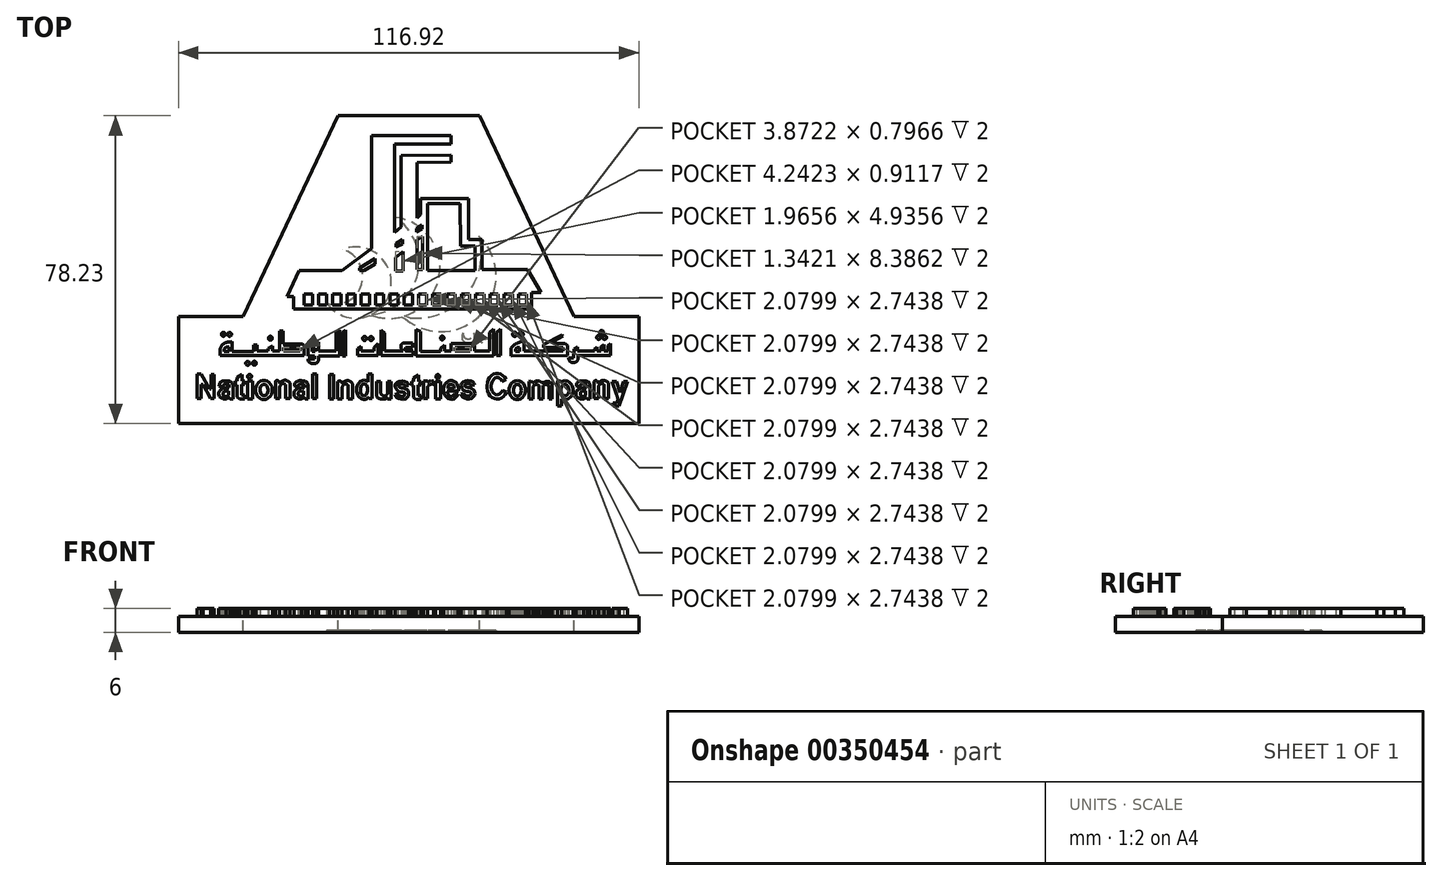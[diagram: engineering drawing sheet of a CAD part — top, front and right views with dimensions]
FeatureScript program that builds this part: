
annotation { "Feature Type Name" : "Feature", "Feature Type Description" : "" }
export const myFeature = defineFeature(function(context is Context, id is Id, definition is map)
    precondition{}
    {
        {
            var Q0;
            Q0=qCreatedBy(makeId("Top.planeOp"),FACE);
            var sketch = newSketch(context, id + "F0", { "sketchPlane" : qUnion([Q0])});
            skCircle(sketch, "E0", {"center": v(48.24, -1.08) * mm, "radius": 0.5 * mm});
            skLineSegment(sketch, "E1", {"start": v(48.24, -1.08) * mm, "end": v(49, 0.22) * mm, "construction": true});
            skLineSegment(sketch, "E2", {"start": v(49, 0.22) * mm, "end": v(49.74, -1.08) * mm, "construction": true});
            skLineSegment(sketch, "E3", {"start": v(49.74, -1.08) * mm, "end": v(48.24, -1.08) * mm, "construction": true});
            skCircle(sketch, "E4", {"center": v(49, 0.22) * mm, "radius": 0.5 * mm});
            skCircle(sketch, "E5", {"center": v(49.74, -1.08) * mm, "radius": 0.5 * mm});
            skLineSegment(sketch, "E6", {"start": v(51.29, -2.6) * mm, "end": v(51.29, -5.68) * mm});
            skLineSegment(sketch, "E7", {"start": v(51.29, -5.68) * mm, "end": v(43.03, -5.68) * mm});
            skLineSegment(sketch, "E8", {"start": v(43.03, -5.68) * mm, "end": v(43.03, -6.28) * mm});
            skArc(sketch, "E9", {"start": v(40.6, -6.28) * mm, "mid": v(41.82, -7.5) * mm, "end": v(43.03, -6.28) * mm});
            skLineSegment(sketch, "E10", {"start": v(51.29, -2.6) * mm, "end": v(50.58, -3.14) * mm});
            skLineSegment(sketch, "E11", {"start": v(50.58, -3.14) * mm, "end": v(50.58, -4.57) * mm});
            skLineSegment(sketch, "E12", {"start": v(50.58, -4.57) * mm, "end": v(49.56, -4.57) * mm});
            skLineSegment(sketch, "E13", {"start": v(49.56, -4.57) * mm, "end": v(49.56, -2.85) * mm});
            skLineSegment(sketch, "E14", {"start": v(49.56, -2.85) * mm, "end": v(48.86, -3.4) * mm});
            skLineSegment(sketch, "E15", {"start": v(48.86, -3.4) * mm, "end": v(48.86, -4.57) * mm});
            skLineSegment(sketch, "E16", {"start": v(48.86, -4.57) * mm, "end": v(47.84, -4.57) * mm});
            skLineSegment(sketch, "E17", {"start": v(47.84, -4.57) * mm, "end": v(47.84, -3.53) * mm});
            skLineSegment(sketch, "E18", {"start": v(47.84, -3.53) * mm, "end": v(47.13, -4.08) * mm});
            skLineSegment(sketch, "E19", {"start": v(47.13, -4.08) * mm, "end": v(47.13, -4.57) * mm});
            skLineSegment(sketch, "E20", {"start": v(47.13, -4.57) * mm, "end": v(43.03, -4.57) * mm});
            skLineSegment(sketch, "E21", {"start": v(43.03, -4.57) * mm, "end": v(42.85, -4.57) * mm});
            skLineSegment(sketch, "E22", {"start": v(42.85, -4.57) * mm, "end": v(42.85, -3.53) * mm});
            skLineSegment(sketch, "E23", {"start": v(42.85, -3.53) * mm, "end": v(41.96, -3.97) * mm});
            skLineSegment(sketch, "E24", {"start": v(41.96, -3.97) * mm, "end": v(41.91, -6.28) * mm});
            skLineSegment(sketch, "E25", {"start": v(41.91, -6.28) * mm, "end": v(40.6, -6.28) * mm});
            skLineSegment(sketch, "E26", {"start": v(47.13, -4.57) * mm, "end": v(47.84, -4.57) * mm, "construction": true});
            skLineSegment(sketch, "E27", {"start": v(48.86, -4.57) * mm, "end": v(49.56, -4.57) * mm, "construction": true});
            skLineSegment(sketch, "E28", {"start": v(50.58, -4.57) * mm, "end": v(51.29, -4.57) * mm, "construction": true});
            skLineSegment(sketch, "E29", {"start": v(39.17, -0.76) * mm, "end": v(36.88, -2.01) * mm});
            skLineSegment(sketch, "E30", {"start": v(36.88, -2.01) * mm, "end": v(36.88, -2.66) * mm});
            skLineSegment(sketch, "E31", {"start": v(36.88, -2.66) * mm, "end": v(39.68, -2.66) * mm});
            skLineSegment(sketch, "E32", {"start": v(39.68, -2.66) * mm, "end": v(40.3, -3.18) * mm});
            skLineSegment(sketch, "E33", {"start": v(40.3, -3.18) * mm, "end": v(40.3, -5.7) * mm});
            skLineSegment(sketch, "E34", {"start": v(40.3, -5.7) * mm, "end": v(26.05, -5.82) * mm});
            skLineSegment(sketch, "E35", {"start": v(26.05, -5.82) * mm, "end": v(26.03, -3.72) * mm});
            skLineSegment(sketch, "E36", {"start": v(39.17, -0.76) * mm, "end": v(38.98, -0.41) * mm});
            skLineSegment(sketch, "E37", {"start": v(38.98, -0.41) * mm, "end": v(34.18, -2.85) * mm});
            skLineSegment(sketch, "E38", {"start": v(34.18, -2.85) * mm, "end": v(34.18, -3.65) * mm});
            skLineSegment(sketch, "E39", {"start": v(34.18, -3.65) * mm, "end": v(39.17, -3.65) * mm});
            skLineSegment(sketch, "E40", {"start": v(39.17, -3.65) * mm, "end": v(39.17, -4.5) * mm});
            skLineSegment(sketch, "E41", {"start": v(39.17, -4.5) * mm, "end": v(29.33, -4.5) * mm});
            skLineSegment(sketch, "E42", {"start": v(29.33, -4.5) * mm, "end": v(29.33, -2.06) * mm});
            skCircle(sketch, "E43", {"center": v(28.57, -0.28) * mm, "radius": 0.55 * mm});
            skCircle(sketch, "E44", {"center": v(26.92, -0.3) * mm, "radius": 0.55 * mm});
            skFitSpline(sketch, "E45", {"points": [v(26.03, -3.72) * mm, v(26.74, -2.98) * mm, v(27.83, -2.4) * mm, v(28.7, -2.13) * mm, v(29.33, -2.06) * mm], "startDerivative": vector(2.44, 2.98) * mm, "endDerivative": vector(2.97, 0.2) * mm});
            skLineSegment(sketch, "E46", {"start": v(23.3, 1.06) * mm, "end": v(22.3, 0.2) * mm});
            skLineSegment(sketch, "E47", {"start": v(22.3, 0.2) * mm, "end": v(22.3, -5.68) * mm});
            skLineSegment(sketch, "E48", {"start": v(22.3, -5.68) * mm, "end": v(23.3, -5.68) * mm});
            skLineSegment(sketch, "E49", {"start": v(23.3, -5.68) * mm, "end": v(23.3, 1.06) * mm});
            skLineSegment(sketch, "E50", {"start": v(21.48, 1.06) * mm, "end": v(20.48, 0.2) * mm});
            skLineSegment(sketch, "E51", {"start": v(20.48, 0.2) * mm, "end": v(20.48, -4.58) * mm});
            skLineSegment(sketch, "E52", {"start": v(20.48, -4.58) * mm, "end": v(16.7, -4.58) * mm});
            skLineSegment(sketch, "E53", {"start": v(16.7, -4.58) * mm, "end": v(16.7, -2.63) * mm});
            skLineSegment(sketch, "E54", {"start": v(16.7, -2.63) * mm, "end": v(10.79, -2.63) * mm});
            skLineSegment(sketch, "E55", {"start": v(10.79, -2.63) * mm, "end": v(10.79, -4.58) * mm});
            skLineSegment(sketch, "E56", {"start": v(10.79, -4.58) * mm, "end": v(9.15, -4.58) * mm});
            skLineSegment(sketch, "E57", {"start": v(9.15, -4.58) * mm, "end": v(9.15, -3.05) * mm});
            skLineSegment(sketch, "E58", {"start": v(9.15, -3.05) * mm, "end": v(8.13, -3.92) * mm});
            skLineSegment(sketch, "E59", {"start": v(8.13, -3.92) * mm, "end": v(8.13, -4.62) * mm});
            skLineSegment(sketch, "E60", {"start": v(8.13, -4.62) * mm, "end": v(2.96, -4.62) * mm});
            skLineSegment(sketch, "E61", {"start": v(2.96, -4.62) * mm, "end": v(2.96, 0.45) * mm});
            skLineSegment(sketch, "E62", {"start": v(2.96, 0.45) * mm, "end": v(1.87, 0.89) * mm});
            skLineSegment(sketch, "E63", {"start": v(1.87, 0.89) * mm, "end": v(1.87, -5.75) * mm});
            skLineSegment(sketch, "E64", {"start": v(1.87, -5.75) * mm, "end": v(21.48, -5.75) * mm});
            skLineSegment(sketch, "E65", {"start": v(21.48, -5.75) * mm, "end": v(21.48, 1.06) * mm});
            skCircle(sketch, "E66", {"center": v(8.49, -1.21) * mm, "radius": 0.47 * mm});
            skLineSegment(sketch, "E67", {"start": v(11.74, -4.47) * mm, "end": v(11.74, -3.67) * mm});
            skLineSegment(sketch, "E68", {"start": v(11.74, -3.67) * mm, "end": v(15.61, -3.67) * mm});
            skLineSegment(sketch, "E69", {"start": v(15.61, -3.67) * mm, "end": v(15.61, -4.47) * mm});
            skLineSegment(sketch, "E70", {"start": v(15.61, -4.47) * mm, "end": v(11.74, -4.47) * mm});
            skLineSegment(sketch, "E71", {"start": v(0.99, -2.48) * mm, "end": v(-1.42, -2.48) * mm});
            skLineSegment(sketch, "E72", {"start": v(0.99, -2.48) * mm, "end": v(0.99, -3.64) * mm});
            skLineSegment(sketch, "E73", {"start": v(0.99, -3.64) * mm, "end": v(-0.78, -3.64) * mm});
            skFitSpline(sketch, "E74", {"points": [v(-1.42, -2.48) * mm, v(-1.9, -2.92) * mm, v(-1.95, -3.8) * mm, v(-1.42, -4.55) * mm], "startDerivative": vector(-1.87, -1.2) * mm, "endDerivative": vector(1.85, -1.92) * mm});
            skFitSpline(sketch, "E75", {"points": [v(-0.78, -3.64) * mm, v(-0.95, -4.14) * mm, v(-0.78, -4.58) * mm], "startDerivative": vector(-0.53, -0.99) * mm, "endDerivative": vector(0.54, -0.9) * mm});
            skLineSegment(sketch, "E76", {"start": v(-0.78, -4.58) * mm, "end": v(1.11, -4.58) * mm});
            skLineSegment(sketch, "E77", {"start": v(1.11, -4.58) * mm, "end": v(1.11, -5.7) * mm});
            skLineSegment(sketch, "E78", {"start": v(1.11, -5.7) * mm, "end": v(-7.1, -5.7) * mm});
            skLineSegment(sketch, "E79", {"start": v(-7.1, -5.7) * mm, "end": v(-7.1, 0.87) * mm});
            skLineSegment(sketch, "E80", {"start": v(-7.1, 0.87) * mm, "end": v(-6.1, 0.09) * mm});
            skLineSegment(sketch, "E81", {"start": v(-6.1, 0.09) * mm, "end": v(-6.1, -4.58) * mm});
            skLineSegment(sketch, "E82", {"start": v(-6.1, -4.58) * mm, "end": v(-1.42, -4.55) * mm});
            skLineSegment(sketch, "E83", {"start": v(-7.78, -2.61) * mm, "end": v(-8.87, -3.6) * mm});
            skLineSegment(sketch, "E84", {"start": v(-8.87, -3.6) * mm, "end": v(-8.87, -4.55) * mm});
            skLineSegment(sketch, "E85", {"start": v(-8.87, -4.55) * mm, "end": v(-12.15, -4.55) * mm});
            skLineSegment(sketch, "E86", {"start": v(-12.15, -4.55) * mm, "end": v(-12.15, -3.32) * mm});
            skLineSegment(sketch, "E87", {"start": v(-12.15, -3.32) * mm, "end": v(-13.02, -3.88) * mm});
            skLineSegment(sketch, "E88", {"start": v(-13.02, -3.88) * mm, "end": v(-13.02, -5.71) * mm});
            skLineSegment(sketch, "E89", {"start": v(-13.02, -5.71) * mm, "end": v(-7.78, -5.71) * mm});
            skLineSegment(sketch, "E90", {"start": v(-7.78, -5.71) * mm, "end": v(-7.78, -2.61) * mm});
            skCircle(sketch, "E91", {"center": v(-9.58, -1.38) * mm, "radius": 0.5 * mm});
            skCircle(sketch, "E92", {"center": v(-11.22, -1.35) * mm, "radius": 0.5 * mm});
            skLineSegment(sketch, "E93", {"start": v(-16, 0.78) * mm, "end": v(-16, -5.74) * mm});
            skLineSegment(sketch, "E94", {"start": v(-16, -5.74) * mm, "end": v(-16.83, -5.74) * mm});
            skLineSegment(sketch, "E95", {"start": v(-16.83, -5.74) * mm, "end": v(-16.83, 0.25) * mm});
            skLineSegment(sketch, "E96", {"start": v(-16.83, 0.25) * mm, "end": v(-16, 0.78) * mm});
            skLineSegment(sketch, "E97", {"start": v(-17.63, 0.78) * mm, "end": v(-17.63, -5.74) * mm});
            skLineSegment(sketch, "E98", {"start": v(-17.63, -5.74) * mm, "end": v(-22.85, -5.74) * mm});
            skLineSegment(sketch, "E99", {"start": v(-22.85, -5.74) * mm, "end": v(-22.85, -6.67) * mm});
            skLineSegment(sketch, "E100", {"start": v(-17.63, 0.78) * mm, "end": v(-18.48, 0.25) * mm});
            skLineSegment(sketch, "E101", {"start": v(-18.48, 0.25) * mm, "end": v(-18.48, -4.5) * mm});
            skLineSegment(sketch, "E102", {"start": v(-18.48, -4.5) * mm, "end": v(-22.88, -4.5) * mm});
            skLineSegment(sketch, "E103", {"start": v(-22.88, -4.5) * mm, "end": v(-22.88, -2.25) * mm});
            skFitSpline(sketch, "E104", {"points": [v(-22.88, -2.25) * mm, v(-24.47, -2.52) * mm, v(-25.6, -3.51) * mm], "startDerivative": vector(-3.34, -0.16) * mm, "endDerivative": vector(-2.1, -2.38) * mm});
            skLineSegment(sketch, "E105", {"start": v(-25.6, -3.51) * mm, "end": v(-25.6, -5.85) * mm});
            skLineSegment(sketch, "E106", {"start": v(-25.6, -5.85) * mm, "end": v(-23.95, -5.85) * mm});
            skLineSegment(sketch, "E107", {"start": v(-23.95, -5.85) * mm, "end": v(-23.95, -6.54) * mm});
            skLineSegment(sketch, "E108", {"start": v(-23.95, -6.54) * mm, "end": v(-25.6, -6.54) * mm});
            skFitSpline(sketch, "E109", {"points": [v(-25.6, -6.54) * mm, v(-25.35, -7.3) * mm, v(-24.14, -7.74) * mm, v(-23.17, -7.4) * mm, v(-22.85, -6.67) * mm], "startDerivative": vector(0.39, -3.57) * mm, "endDerivative": vector(0.93, 3.52) * mm});
            skLineSegment(sketch, "E110", {"start": v(-23.83, -3.75) * mm, "end": v(-23.83, -4.67) * mm});
            skLineSegment(sketch, "E111", {"start": v(-23.83, -4.67) * mm, "end": v(-24.61, -4.67) * mm});
            skLineSegment(sketch, "E112", {"start": v(-24.61, -4.67) * mm, "end": v(-24.61, -3.75) * mm});
            skLineSegment(sketch, "E113", {"start": v(-24.61, -3.75) * mm, "end": v(-23.83, -3.75) * mm});
            skLineSegment(sketch, "E114", {"start": v(-31.85, -3.65) * mm, "end": v(-27.6, -3.65) * mm});
            skLineSegment(sketch, "E115", {"start": v(-27.6, -3.65) * mm, "end": v(-27.6, -4.56) * mm});
            skLineSegment(sketch, "E116", {"start": v(-27.6, -4.56) * mm, "end": v(-31.85, -4.56) * mm});
            skLineSegment(sketch, "E117", {"start": v(-31.85, -4.56) * mm, "end": v(-31.85, -3.65) * mm});
            skCircle(sketch, "E118", {"center": v(-39.24, -7.62) * mm, "radius": 0.5 * mm});
            skCircle(sketch, "E119", {"center": v(-40.93, -7.65) * mm, "radius": 0.5 * mm});
            skCircle(sketch, "E120", {"center": v(-35.16, -1.27) * mm, "radius": 0.5 * mm});
            skCircle(sketch, "E121", {"center": v(-45.52, -0.3) * mm, "radius": 0.5 * mm});
            skCircle(sketch, "E122", {"center": v(-47.11, -0.3) * mm, "radius": 0.5 * mm});
            skLineSegment(sketch, "E123", {"start": v(28.2, -3.6) * mm, "end": v(28.2, -4.62) * mm});
            skLineSegment(sketch, "E124", {"start": v(28.2, -4.62) * mm, "end": v(27.09, -4.62) * mm});
            skLineSegment(sketch, "E125", {"start": v(27.09, -4.62) * mm, "end": v(27.09, -3.97) * mm});
            skLineSegment(sketch, "E126", {"start": v(27.09, -3.97) * mm, "end": v(27.54, -3.6) * mm});
            skLineSegment(sketch, "E127", {"start": v(27.54, -3.6) * mm, "end": v(28.2, -3.6) * mm});
            skLineSegment(sketch, "E128", {"start": v(-31.92, 0.6) * mm, "end": v(-31.92, -2.78) * mm});
            skLineSegment(sketch, "E129", {"start": v(-31.92, -2.78) * mm, "end": v(-27.02, -2.78) * mm});
            skLineSegment(sketch, "E130", {"start": v(-27.02, -2.78) * mm, "end": v(-26.56, -3.22) * mm});
            skLineSegment(sketch, "E131", {"start": v(-26.56, -3.22) * mm, "end": v(-26.56, -5.66) * mm});
            skLineSegment(sketch, "E132", {"start": v(-26.56, -5.66) * mm, "end": v(-47.89, -5.66) * mm});
            skLineSegment(sketch, "E133", {"start": v(-47.89, -5.66) * mm, "end": v(-47.89, -3.85) * mm});
            skFitSpline(sketch, "E134", {"points": [v(-47.89, -3.85) * mm, v(-47.42, -3.03) * mm, v(-46.55, -2.42) * mm, v(-44.91, -2.17) * mm], "startDerivative": vector(1.34, 2.92) * mm, "endDerivative": vector(4.5, 0.32) * mm});
            skLineSegment(sketch, "E135", {"start": v(-44.91, -2.17) * mm, "end": v(-44.91, -4.6) * mm});
            skLineSegment(sketch, "E136", {"start": v(-44.91, -4.6) * mm, "end": v(-39.44, -4.6) * mm});
            skLineSegment(sketch, "E137", {"start": v(-39.44, -4.6) * mm, "end": v(-39.44, -3) * mm});
            skLineSegment(sketch, "E138", {"start": v(-39.44, -3) * mm, "end": v(-38.57, -3) * mm});
            skLineSegment(sketch, "E139", {"start": v(-38.57, -3) * mm, "end": v(-38.57, -4.52) * mm});
            skLineSegment(sketch, "E140", {"start": v(-38.57, -4.52) * mm, "end": v(-35.7, -4.52) * mm});
            skLineSegment(sketch, "E141", {"start": v(-35.7, -4.52) * mm, "end": v(-35.7, -3.94) * mm});
            skLineSegment(sketch, "E142", {"start": v(-35.7, -3.94) * mm, "end": v(-34.6, -3.2) * mm});
            skLineSegment(sketch, "E143", {"start": v(-34.6, -3.2) * mm, "end": v(-34.6, -4.52) * mm});
            skLineSegment(sketch, "E144", {"start": v(-34.6, -4.52) * mm, "end": v(-32.85, -4.52) * mm});
            skLineSegment(sketch, "E145", {"start": v(-32.85, -4.52) * mm, "end": v(-32.85, 0.6) * mm});
            skLineSegment(sketch, "E146", {"start": v(-32.85, 0.6) * mm, "end": v(-31.92, 0.6) * mm});
            skLineSegment(sketch, "E147", {"start": v(-45.68, -3.54) * mm, "end": v(-45.68, -4.68) * mm});
            skLineSegment(sketch, "E148", {"start": v(-45.68, -4.68) * mm, "end": v(-46.94, -4.68) * mm});
            skLineSegment(sketch, "E149", {"start": v(-46.94, -4.68) * mm, "end": v(-46.94, -3.97) * mm});
            skLineSegment(sketch, "E150", {"start": v(-46.94, -3.97) * mm, "end": v(-46.4, -3.54) * mm});
            skLineSegment(sketch, "E151", {"start": v(-46.4, -3.54) * mm, "end": v(-45.68, -3.54) * mm});
            skLineSegment(sketch, "E152", {"start": v(-53.75, -16.57) * mm, "end": v(-53.75, -10.42) * mm});
            skLineSegment(sketch, "E153", {"start": v(-53.75, -10.42) * mm, "end": v(-52.77, -10.42) * mm});
            skLineSegment(sketch, "E154", {"start": v(-52.77, -10.42) * mm, "end": v(-50.6, -14.14) * mm});
            skLineSegment(sketch, "E155", {"start": v(-50.6, -14.14) * mm, "end": v(-50.16, -14.14) * mm});
            skLineSegment(sketch, "E156", {"start": v(-50.16, -14.14) * mm, "end": v(-50.16, -10.46) * mm});
            skLineSegment(sketch, "E157", {"start": v(-50.16, -10.46) * mm, "end": v(-49.4, -10.46) * mm});
            skLineSegment(sketch, "E158", {"start": v(-49.4, -10.46) * mm, "end": v(-49.4, -16.57) * mm});
            skLineSegment(sketch, "E159", {"start": v(-49.4, -16.57) * mm, "end": v(-50.4, -16.57) * mm});
            skLineSegment(sketch, "E160", {"start": v(-50.4, -16.57) * mm, "end": v(-52.24, -12.99) * mm});
            skLineSegment(sketch, "E161", {"start": v(-52.24, -12.99) * mm, "end": v(-52.71, -12.99) * mm});
            skLineSegment(sketch, "E162", {"start": v(-52.71, -12.99) * mm, "end": v(-52.71, -16.57) * mm});
            skLineSegment(sketch, "E163", {"start": v(-52.71, -16.57) * mm, "end": v(-53.75, -16.57) * mm});
            skLineSegment(sketch, "E164", {"start": v(-45.82, -14.69) * mm, "end": v(-45.82, -15.71) * mm});
            skFitSpline(sketch, "E165", {"points": [v(-45.82, -15.71) * mm, v(-46.28, -16.01) * mm, v(-47.04, -15.86) * mm, v(-47.16, -15.4) * mm, v(-47.11, -15.03) * mm, v(-46.68, -14.73) * mm, v(-46.18, -14.62) * mm], "startDerivative": vector(-2.15, -2.28) * mm, "endDerivative": vector(2.93, 1.5) * mm});
            skFitSpline(sketch, "E166", {"points": [v(-46.18, -14.62) * mm, v(-45.82, -14.69) * mm], "startDerivative": vector(0.32, -0.12) * mm, "endDerivative": vector(0.32, -0.12) * mm});
            skLineSegment(sketch, "E167", {"start": v(-44.69, -13.02) * mm, "end": v(-44.69, -16.74) * mm});
            skLineSegment(sketch, "E168", {"start": v(-44.69, -16.74) * mm, "end": v(-45.34, -16.74) * mm});
            skFitSpline(sketch, "E169", {"points": [v(-45.34, -16.74) * mm, v(-45.71, -16.4) * mm, v(-46.37, -16.74) * mm], "startDerivative": vector(-0.73, 1.05) * mm, "endDerivative": vector(-1.3, -0.98) * mm});
            skFitSpline(sketch, "E170", {"points": [v(-46.37, -16.74) * mm, v(-47.07, -16.74) * mm, v(-47.72, -16.42) * mm, v(-48.19, -15.96) * mm, v(-48.23, -15.03) * mm, v(-47.93, -14.5) * mm, v(-47.53, -14.19) * mm, v(-47.32, -14.1) * mm, v(-47.04, -13.97) * mm, v(-46.24, -13.85) * mm], "startDerivative": vector(-5.8, -0.65) * mm, "endDerivative": vector(6.93, 0.53) * mm});
            skLineSegment(sketch, "E171", {"start": v(-46.24, -13.85) * mm, "end": v(-45.6, -13.85) * mm});
            skLineSegment(sketch, "E172", {"start": v(-45.6, -13.85) * mm, "end": v(-45.6, -13.13) * mm});
            skFitSpline(sketch, "E173", {"points": [v(-44.69, -13.02) * mm, v(-44.95, -12.55) * mm, v(-45.52, -12.2) * mm, v(-46.4, -12.09) * mm, v(-47.26, -12.16) * mm, v(-47.99, -12.65) * mm, v(-48.13, -13.13) * mm, v(-48.14, -13.47) * mm], "startDerivative": vector(-1.65, 3.82) * mm, "endDerivative": vector(-0.04, -3.2) * mm});
            skFitSpline(sketch, "E174", {"points": [v(-48.14, -13.47) * mm, v(-47.32, -13.47) * mm, v(-47.17, -13.26) * mm, v(-46.9, -13.02) * mm, v(-46.4, -12.9) * mm, v(-45.9, -12.96) * mm, v(-45.6, -13.13) * mm], "startDerivative": vector(4.5, -0.54) * mm, "endDerivative": vector(1.87, -1.28) * mm});
            skLineSegment(sketch, "E175", {"start": v(-40.98, -12.19) * mm, "end": v(-40.98, -16.68) * mm});
            skLineSegment(sketch, "E176", {"start": v(-40.98, -16.68) * mm, "end": v(-39.74, -16.68) * mm});
            skLineSegment(sketch, "E177", {"start": v(-39.74, -16.68) * mm, "end": v(-39.74, -12.19) * mm});
            skLineSegment(sketch, "E178", {"start": v(-39.74, -12.19) * mm, "end": v(-40.98, -12.19) * mm});
            skCircle(sketch, "E179", {"center": v(-40.45, -10.98) * mm, "radius": 0.5 * mm});
            skEllipse(sketch, "E180", {"center": v(-36.8, -14.42) * mm, "majorRadius": 1.44 * mm, "minorRadius": 1.03 * mm, "majorAxis": v(0, -1)});
            skEllipse(sketch, "E181", {"center": v(-36.8, -14.42) * mm, "majorRadius": 2.46 * mm, "minorRadius": 2.13 * mm, "majorAxis": v(0, -1)});
            skLineSegment(sketch, "E182", {"start": v(-33.88, -12.24) * mm, "end": v(-33.88, -16.58) * mm});
            skLineSegment(sketch, "E183", {"start": v(-33.88, -16.58) * mm, "end": v(-32.78, -16.58) * mm});
            skLineSegment(sketch, "E184", {"start": v(-32.78, -16.58) * mm, "end": v(-32.78, -13.6) * mm});
            skFitSpline(sketch, "E185", {"points": [v(-32.78, -13.6) * mm, v(-32.45, -13.03) * mm, v(-31.9, -12.78) * mm, v(-31.27, -13.08) * mm], "startDerivative": vector(0.82, 1.83) * mm, "endDerivative": vector(1.83, -1.27) * mm});
            skLineSegment(sketch, "E186", {"start": v(-31.27, -13.08) * mm, "end": v(-31.27, -16.58) * mm});
            skLineSegment(sketch, "E187", {"start": v(-31.27, -16.58) * mm, "end": v(-30.12, -16.58) * mm});
            skLineSegment(sketch, "E188", {"start": v(-30.12, -16.58) * mm, "end": v(-30.12, -12.81) * mm});
            skFitSpline(sketch, "E189", {"points": [v(-33.88, -12.24) * mm, v(-33.45, -12) * mm, v(-32.9, -12.34) * mm, v(-32.8, -12.73) * mm], "startDerivative": vector(1.19, 1.08) * mm, "endDerivative": vector(0.02, -1.32) * mm});
            skFitSpline(sketch, "E190", {"points": [v(-30.12, -12.81) * mm, v(-30.6, -12.24) * mm, v(-31.34, -11.95) * mm, v(-31.81, -12) * mm, v(-32.3, -12.24) * mm, v(-32.8, -12.73) * mm], "startDerivative": vector(-1.86, 2.95) * mm, "endDerivative": vector(-2.36, -2.6) * mm});
            skLineSegment(sketch, "E191", {"start": v(-26.73, -14.67) * mm, "end": v(-26.73, -15.7) * mm});
            skFitSpline(sketch, "E192", {"points": [v(-26.73, -15.7) * mm, v(-27.2, -16) * mm, v(-27.96, -15.85) * mm, v(-28.07, -15.4) * mm, v(-28.03, -15.02) * mm, v(-27.6, -14.72) * mm, v(-27.1, -14.6) * mm], "startDerivative": vector(-2.15, -2.28) * mm, "endDerivative": vector(2.93, 1.5) * mm});
            skFitSpline(sketch, "E193", {"points": [v(-27.1, -14.6) * mm, v(-26.73, -14.67) * mm], "startDerivative": vector(0.32, -0.12) * mm, "endDerivative": vector(0.32, -0.12) * mm});
            skLineSegment(sketch, "E194", {"start": v(-25.6, -13.01) * mm, "end": v(-25.6, -16.73) * mm});
            skLineSegment(sketch, "E195", {"start": v(-25.6, -16.73) * mm, "end": v(-26.26, -16.73) * mm});
            skFitSpline(sketch, "E196", {"points": [v(-26.26, -16.73) * mm, v(-26.63, -16.4) * mm, v(-27.29, -16.73) * mm], "startDerivative": vector(-0.73, 1.05) * mm, "endDerivative": vector(-1.3, -0.98) * mm});
            skFitSpline(sketch, "E197", {"points": [v(-27.29, -16.73) * mm, v(-27.98, -16.73) * mm, v(-28.64, -16.4) * mm, v(-29.1, -15.95) * mm, v(-29.15, -15.02) * mm, v(-28.85, -14.49) * mm, v(-28.44, -14.18) * mm, v(-28.24, -14.1) * mm, v(-27.96, -13.96) * mm, v(-27.16, -13.84) * mm], "startDerivative": vector(-5.8, -0.65) * mm, "endDerivative": vector(6.93, 0.53) * mm});
            skLineSegment(sketch, "E198", {"start": v(-27.16, -13.84) * mm, "end": v(-26.51, -13.84) * mm});
            skLineSegment(sketch, "E199", {"start": v(-26.51, -13.84) * mm, "end": v(-26.51, -13.11) * mm});
            skFitSpline(sketch, "E200", {"points": [v(-25.6, -13.01) * mm, v(-25.87, -12.54) * mm, v(-26.43, -12.18) * mm, v(-27.31, -12.07) * mm, v(-28.18, -12.14) * mm, v(-28.9, -12.64) * mm, v(-29.04, -13.11) * mm, v(-29.06, -13.46) * mm], "startDerivative": vector(-1.65, 3.82) * mm, "endDerivative": vector(-0.04, -3.2) * mm});
            skFitSpline(sketch, "E201", {"points": [v(-29.06, -13.46) * mm, v(-28.24, -13.46) * mm, v(-28.09, -13.25) * mm, v(-27.82, -13.01) * mm, v(-27.31, -12.9) * mm, v(-26.81, -12.95) * mm, v(-26.51, -13.11) * mm], "startDerivative": vector(4.5, -0.54) * mm, "endDerivative": vector(1.87, -1.28) * mm});
            skLineSegment(sketch, "E202", {"start": v(-18.03, -12.33) * mm, "end": v(-18.03, -16.68) * mm});
            skLineSegment(sketch, "E203", {"start": v(-18.03, -16.68) * mm, "end": v(-16.94, -16.68) * mm});
            skLineSegment(sketch, "E204", {"start": v(-16.94, -16.68) * mm, "end": v(-16.94, -13.7) * mm});
            skFitSpline(sketch, "E205", {"points": [v(-16.94, -13.7) * mm, v(-16.6, -13.13) * mm, v(-16.06, -12.88) * mm, v(-15.42, -13.18) * mm], "startDerivative": vector(0.82, 1.83) * mm, "endDerivative": vector(1.83, -1.27) * mm});
            skLineSegment(sketch, "E206", {"start": v(-15.42, -13.18) * mm, "end": v(-15.42, -16.68) * mm});
            skLineSegment(sketch, "E207", {"start": v(-15.42, -16.68) * mm, "end": v(-14.28, -16.68) * mm});
            skLineSegment(sketch, "E208", {"start": v(-14.28, -16.68) * mm, "end": v(-14.28, -12.91) * mm});
            skFitSpline(sketch, "E209", {"points": [v(-18.03, -12.33) * mm, v(-17.6, -12.1) * mm, v(-17.05, -12.44) * mm, v(-16.96, -12.83) * mm], "startDerivative": vector(1.19, 1.08) * mm, "endDerivative": vector(0.02, -1.32) * mm});
            skFitSpline(sketch, "E210", {"points": [v(-14.28, -12.91) * mm, v(-14.75, -12.33) * mm, v(-15.5, -12.04) * mm, v(-15.97, -12.1) * mm, v(-16.45, -12.33) * mm, v(-16.96, -12.83) * mm], "startDerivative": vector(-1.86, 2.95) * mm, "endDerivative": vector(-2.36, -2.6) * mm});
            skLineSegment(sketch, "E211", {"start": v(-23.45, -10.43) * mm, "end": v(-23.45, -16.65) * mm});
            skLineSegment(sketch, "E212", {"start": v(-23.45, -16.65) * mm, "end": v(-24.5, -16.65) * mm});
            skLineSegment(sketch, "E213", {"start": v(-24.5, -16.65) * mm, "end": v(-24.5, -10.43) * mm});
            skLineSegment(sketch, "E214", {"start": v(-24.5, -10.43) * mm, "end": v(-23.45, -10.43) * mm});
            skLineSegment(sketch, "E215", {"start": v(-19.09, -10.51) * mm, "end": v(-19.09, -16.73) * mm});
            skLineSegment(sketch, "E216", {"start": v(-19.09, -16.73) * mm, "end": v(-20.14, -16.73) * mm});
            skLineSegment(sketch, "E217", {"start": v(-20.14, -16.73) * mm, "end": v(-20.14, -10.51) * mm});
            skLineSegment(sketch, "E218", {"start": v(-20.14, -10.51) * mm, "end": v(-19.09, -10.51) * mm});
            skLineSegment(sketch, "E219", {"start": v(-42.4, -10.53) * mm, "end": v(-43.58, -11.24) * mm});
            skLineSegment(sketch, "E220", {"start": v(-43.58, -11.24) * mm, "end": v(-43.58, -12.11) * mm});
            skLineSegment(sketch, "E221", {"start": v(-43.58, -12.11) * mm, "end": v(-44.07, -12.11) * mm});
            skLineSegment(sketch, "E222", {"start": v(-44.07, -12.11) * mm, "end": v(-44.07, -13.14) * mm});
            skLineSegment(sketch, "E223", {"start": v(-44.07, -13.14) * mm, "end": v(-43.61, -13.14) * mm});
            skLineSegment(sketch, "E224", {"start": v(-43.61, -13.14) * mm, "end": v(-43.61, -16.26) * mm});
            skLineSegment(sketch, "E225", {"start": v(-43.61, -16.26) * mm, "end": v(-42.98, -16.7) * mm});
            skLineSegment(sketch, "E226", {"start": v(-42.98, -16.7) * mm, "end": v(-41.67, -16.7) * mm});
            skLineSegment(sketch, "E227", {"start": v(-41.67, -16.7) * mm, "end": v(-41.67, -15.74) * mm});
            skLineSegment(sketch, "E228", {"start": v(-41.67, -15.74) * mm, "end": v(-42.42, -15.74) * mm});
            skLineSegment(sketch, "E229", {"start": v(-42.42, -15.74) * mm, "end": v(-42.42, -13.06) * mm});
            skLineSegment(sketch, "E230", {"start": v(-42.42, -13.06) * mm, "end": v(-41.66, -13.06) * mm});
            skLineSegment(sketch, "E231", {"start": v(-41.66, -13.06) * mm, "end": v(-41.66, -12.11) * mm});
            skLineSegment(sketch, "E232", {"start": v(-41.66, -12.11) * mm, "end": v(-42.4, -12.11) * mm});
            skLineSegment(sketch, "E233", {"start": v(-42.4, -12.11) * mm, "end": v(-42.4, -10.53) * mm});
            skLineSegment(sketch, "E234", {"start": v(2.43, -10.67) * mm, "end": v(1.25, -11.37) * mm});
            skLineSegment(sketch, "E235", {"start": v(1.25, -11.37) * mm, "end": v(1.25, -12.25) * mm});
            skLineSegment(sketch, "E236", {"start": v(1.25, -12.25) * mm, "end": v(0.77, -12.25) * mm});
            skLineSegment(sketch, "E237", {"start": v(0.77, -12.25) * mm, "end": v(0.77, -13.28) * mm});
            skLineSegment(sketch, "E238", {"start": v(0.77, -13.28) * mm, "end": v(1.22, -13.28) * mm});
            skLineSegment(sketch, "E239", {"start": v(1.22, -13.28) * mm, "end": v(1.22, -16.4) * mm});
            skLineSegment(sketch, "E240", {"start": v(1.22, -16.4) * mm, "end": v(1.86, -16.84) * mm});
            skLineSegment(sketch, "E241", {"start": v(1.86, -16.84) * mm, "end": v(3.16, -16.84) * mm});
            skLineSegment(sketch, "E242", {"start": v(3.16, -16.84) * mm, "end": v(3.16, -15.88) * mm});
            skLineSegment(sketch, "E243", {"start": v(3.16, -15.88) * mm, "end": v(2.42, -15.88) * mm});
            skLineSegment(sketch, "E244", {"start": v(2.42, -15.88) * mm, "end": v(2.42, -13.2) * mm});
            skLineSegment(sketch, "E245", {"start": v(2.42, -13.2) * mm, "end": v(3.18, -13.2) * mm});
            skLineSegment(sketch, "E246", {"start": v(3.18, -13.2) * mm, "end": v(3.18, -12.25) * mm});
            skLineSegment(sketch, "E247", {"start": v(3.18, -12.25) * mm, "end": v(2.43, -12.25) * mm});
            skLineSegment(sketch, "E248", {"start": v(2.43, -12.25) * mm, "end": v(2.43, -10.67) * mm});
            skLineSegment(sketch, "E249", {"start": v(44.92, -14.69) * mm, "end": v(44.92, -15.71) * mm});
            skFitSpline(sketch, "E250", {"points": [v(44.92, -15.71) * mm, v(44.46, -16.01) * mm, v(43.7, -15.86) * mm, v(43.58, -15.4) * mm, v(43.63, -15.03) * mm, v(44.06, -14.73) * mm, v(44.56, -14.62) * mm], "startDerivative": vector(-2.15, -2.28) * mm, "endDerivative": vector(2.93, 1.5) * mm});
            skFitSpline(sketch, "E251", {"points": [v(44.56, -14.62) * mm, v(44.92, -14.69) * mm], "startDerivative": vector(0.32, -0.12) * mm, "endDerivative": vector(0.32, -0.12) * mm});
            skLineSegment(sketch, "E252", {"start": v(46.05, -13.02) * mm, "end": v(46.05, -16.74) * mm});
            skLineSegment(sketch, "E253", {"start": v(46.05, -16.74) * mm, "end": v(45.4, -16.74) * mm});
            skFitSpline(sketch, "E254", {"points": [v(45.4, -16.74) * mm, v(45.03, -16.4) * mm, v(44.37, -16.74) * mm], "startDerivative": vector(-0.73, 1.05) * mm, "endDerivative": vector(-1.3, -0.98) * mm});
            skFitSpline(sketch, "E255", {"points": [v(44.37, -16.74) * mm, v(43.67, -16.74) * mm, v(43.02, -16.42) * mm, v(42.55, -15.96) * mm, v(42.5, -15.03) * mm, v(42.8, -14.5) * mm, v(43.21, -14.19) * mm, v(43.42, -14.1) * mm, v(43.7, -13.97) * mm, v(44.5, -13.85) * mm], "startDerivative": vector(-5.8, -0.65) * mm, "endDerivative": vector(6.93, 0.53) * mm});
            skLineSegment(sketch, "E256", {"start": v(44.5, -13.85) * mm, "end": v(45.14, -13.85) * mm});
            skLineSegment(sketch, "E257", {"start": v(45.14, -13.85) * mm, "end": v(45.14, -13.13) * mm});
            skFitSpline(sketch, "E258", {"points": [v(46.05, -13.02) * mm, v(45.79, -12.55) * mm, v(45.22, -12.2) * mm, v(44.34, -12.09) * mm, v(43.48, -12.16) * mm, v(42.75, -12.65) * mm, v(42.61, -13.13) * mm, v(42.6, -13.47) * mm], "startDerivative": vector(-1.65, 3.82) * mm, "endDerivative": vector(-0.04, -3.2) * mm});
            skFitSpline(sketch, "E259", {"points": [v(42.6, -13.47) * mm, v(43.42, -13.47) * mm, v(43.57, -13.26) * mm, v(43.84, -13.02) * mm, v(44.34, -12.9) * mm, v(44.85, -12.96) * mm, v(45.14, -13.13) * mm], "startDerivative": vector(4.5, -0.54) * mm, "endDerivative": vector(1.87, -1.28) * mm});
            skLineSegment(sketch, "E260", {"start": v(47.05, -12.25) * mm, "end": v(47.05, -16.6) * mm});
            skLineSegment(sketch, "E261", {"start": v(47.05, -16.6) * mm, "end": v(48.15, -16.6) * mm});
            skLineSegment(sketch, "E262", {"start": v(48.15, -16.6) * mm, "end": v(48.15, -13.62) * mm});
            skFitSpline(sketch, "E263", {"points": [v(48.15, -13.62) * mm, v(48.48, -13.05) * mm, v(49.03, -12.8) * mm, v(49.66, -13.1) * mm], "startDerivative": vector(0.82, 1.83) * mm, "endDerivative": vector(1.83, -1.27) * mm});
            skLineSegment(sketch, "E264", {"start": v(49.66, -13.1) * mm, "end": v(49.66, -16.6) * mm});
            skLineSegment(sketch, "E265", {"start": v(49.66, -16.6) * mm, "end": v(50.8, -16.6) * mm});
            skLineSegment(sketch, "E266", {"start": v(50.8, -16.6) * mm, "end": v(50.8, -12.83) * mm});
            skFitSpline(sketch, "E267", {"points": [v(47.05, -12.25) * mm, v(47.48, -12.02) * mm, v(48.03, -12.36) * mm, v(48.12, -12.75) * mm], "startDerivative": vector(1.19, 1.08) * mm, "endDerivative": vector(0.02, -1.32) * mm});
            skFitSpline(sketch, "E268", {"points": [v(50.8, -12.83) * mm, v(50.33, -12.25) * mm, v(49.6, -11.96) * mm, v(49.12, -12.01) * mm, v(48.63, -12.25) * mm, v(48.12, -12.75) * mm], "startDerivative": vector(-1.86, 2.95) * mm, "endDerivative": vector(-2.36, -2.6) * mm});
            skLineSegment(sketch, "E269", {"start": v(55.6, -12.29) * mm, "end": v(53.42, -18.44) * mm});
            skLineSegment(sketch, "E270", {"start": v(53.42, -18.44) * mm, "end": v(51.87, -18.44) * mm});
            skLineSegment(sketch, "E271", {"start": v(51.87, -18.44) * mm, "end": v(51.87, -17.71) * mm});
            skLineSegment(sketch, "E272", {"start": v(51.87, -17.71) * mm, "end": v(52.6, -17.71) * mm});
            skFitSpline(sketch, "E273", {"points": [v(52.6, -17.71) * mm, v(52.9, -17.41) * mm, v(53.1, -16.82) * mm, v(52.98, -16.14) * mm, v(52.76, -15.56) * mm], "startDerivative": vector(1.5, 1.22) * mm, "endDerivative": vector(-0.86, 2.17) * mm});
            skLineSegment(sketch, "E274", {"start": v(52.76, -15.56) * mm, "end": v(51.58, -12.25) * mm});
            skLineSegment(sketch, "E275", {"start": v(51.58, -12.25) * mm, "end": v(52.76, -12.25) * mm});
            skLineSegment(sketch, "E276", {"start": v(52.76, -12.25) * mm, "end": v(53.7, -15.12) * mm});
            skLineSegment(sketch, "E277", {"start": v(53.7, -15.12) * mm, "end": v(54.58, -12.29) * mm});
            skEllipticalArc(sketch, "E278", {});
            skEllipticalArc(sketch, "E279", {});
            skLineSegment(sketch, "E280", {"start": v(23.8, -14.5) * mm, "end": v(24.79, -14.95) * mm});
            skLineSegment(sketch, "E281", {"start": v(23.75, -12.33) * mm, "end": v(24.68, -11.76) * mm});
            skEllipse(sketch, "E282", {"center": v(27.59, -14.48) * mm, "majorRadius": 1.5 * mm, "minorRadius": 1 * mm, "majorAxis": v(0, 1)});
            skEllipse(sketch, "E283", {"center": v(27.59, -14.48) * mm, "majorRadius": 2.42 * mm, "minorRadius": 2.12 * mm, "majorAxis": v(0, 1)});
            skEllipse(sketch, "E284", {"center": v(39.67, -14.48) * mm, "majorRadius": 1.46 * mm, "minorRadius": 1.02 * mm, "majorAxis": v(0, -1)});
            skLineSegment(sketch, "E285", {"start": v(30.5, -16.76) * mm, "end": v(30.5, -12.27) * mm});
            skLineSegment(sketch, "E286", {"start": v(30.5, -12.27) * mm, "end": v(31.09, -12.13) * mm});
            skLineSegment(sketch, "E287", {"start": v(31.09, -12.13) * mm, "end": v(31.5, -12.47) * mm});
            skLineSegment(sketch, "E288", {"start": v(31.5, -12.47) * mm, "end": v(31.88, -12.47) * mm});
            skLineSegment(sketch, "E289", {"start": v(31.88, -12.47) * mm, "end": v(32.2, -12.09) * mm});
            skLineSegment(sketch, "E290", {"start": v(32.2, -12.09) * mm, "end": v(33.27, -12.09) * mm});
            skLineSegment(sketch, "E291", {"start": v(33.27, -12.09) * mm, "end": v(33.73, -12.59) * mm});
            skLineSegment(sketch, "E292", {"start": v(33.73, -12.59) * mm, "end": v(34.34, -12.59) * mm});
            skLineSegment(sketch, "E293", {"start": v(34.34, -12.59) * mm, "end": v(35.4, -12.06) * mm});
            skLineSegment(sketch, "E294", {"start": v(35.4, -12.06) * mm, "end": v(36.43, -12.74) * mm});
            skLineSegment(sketch, "E295", {"start": v(36.43, -12.74) * mm, "end": v(36.43, -16.76) * mm});
            skLineSegment(sketch, "E296", {"start": v(36.43, -16.76) * mm, "end": v(35.62, -16.76) * mm});
            skLineSegment(sketch, "E297", {"start": v(35.62, -16.76) * mm, "end": v(35.62, -13.26) * mm});
            skLineSegment(sketch, "E298", {"start": v(35.62, -13.26) * mm, "end": v(34.94, -12.97) * mm});
            skLineSegment(sketch, "E299", {"start": v(34.94, -12.97) * mm, "end": v(34.13, -13.3) * mm});
            skLineSegment(sketch, "E300", {"start": v(34.13, -13.3) * mm, "end": v(34.13, -16.76) * mm});
            skLineSegment(sketch, "E301", {"start": v(34.13, -16.76) * mm, "end": v(33.07, -16.76) * mm});
            skLineSegment(sketch, "E302", {"start": v(33.07, -16.76) * mm, "end": v(33.07, -13.33) * mm});
            skLineSegment(sketch, "E303", {"start": v(33.07, -13.33) * mm, "end": v(32.7, -13.01) * mm});
            skLineSegment(sketch, "E304", {"start": v(32.7, -13.01) * mm, "end": v(32.03, -13) * mm});
            skLineSegment(sketch, "E305", {"start": v(32.03, -13) * mm, "end": v(31.55, -13.55) * mm});
            skLineSegment(sketch, "E306", {"start": v(31.55, -13.55) * mm, "end": v(31.55, -16.76) * mm});
            skLineSegment(sketch, "E307", {"start": v(31.55, -16.76) * mm, "end": v(30.5, -16.76) * mm});
            skEllipticalArc(sketch, "E308", {});
            skLineSegment(sketch, "E309", {"start": v(38.59, -12.42) * mm, "end": v(38.59, -12.14) * mm});
            skLineSegment(sketch, "E310", {"start": v(38.59, -12.14) * mm, "end": v(37.74, -12.14) * mm});
            skLineSegment(sketch, "E311", {"start": v(37.74, -12.14) * mm, "end": v(37.74, -18.5) * mm});
            skLineSegment(sketch, "E312", {"start": v(37.74, -18.5) * mm, "end": v(38.83, -18.5) * mm});
            skLineSegment(sketch, "E313", {"start": v(38.83, -18.5) * mm, "end": v(38.83, -16.7) * mm});
            skLineSegment(sketch, "E314", {"start": v(54.58, -12.29) * mm, "end": v(55.6, -12.29) * mm});
            skLineSegment(sketch, "E315", {"start": v(6.84, -12.22) * mm, "end": v(6.84, -16.71) * mm});
            skLineSegment(sketch, "E316", {"start": v(6.84, -16.71) * mm, "end": v(8.08, -16.71) * mm});
            skLineSegment(sketch, "E317", {"start": v(8.08, -16.71) * mm, "end": v(8.08, -12.22) * mm});
            skLineSegment(sketch, "E318", {"start": v(8.08, -12.22) * mm, "end": v(6.84, -12.22) * mm});
            skCircle(sketch, "E319", {"center": v(7.37, -11) * mm, "radius": 0.5 * mm});
            skLineSegment(sketch, "E320", {"start": v(-3.54, -15.54) * mm, "end": v(-2.88, -15.38) * mm});
            skLineSegment(sketch, "E321", {"start": v(-0.85, -13.4) * mm, "end": v(-0.06, -13.24) * mm});
            skFitSpline(sketch, "E322", {"points": [v(-0.06, -13.24) * mm, v(-0.3, -12.7) * mm, v(-1.8, -12.12) * mm, v(-3.29, -12.78) * mm, v(-3.47, -13.5) * mm, v(-3.22, -14.19) * mm, v(-2.41, -14.83) * mm, v(-1.45, -14.95) * mm, v(-1.1, -15.15) * mm, v(-0.97, -15.42) * mm, v(-1.15, -15.87) * mm, v(-1.65, -16.06) * mm, v(-2.25, -15.99) * mm, v(-2.88, -15.38) * mm], "startDerivative": vector(-1.49, 8.18) * mm, "endDerivative": vector(-7.28, 8.95) * mm});
            skFitSpline(sketch, "E323", {"points": [v(-0.85, -13.4) * mm, v(-1.19, -13.05) * mm, v(-1.72, -12.91) * mm, v(-2.27, -12.99) * mm, v(-2.57, -13.24) * mm, v(-2.55, -13.52) * mm, v(-2.1, -13.83) * mm, v(-1.35, -13.94) * mm, v(-0.68, -14.23) * mm, v(-0.23, -14.54) * mm, v(-0.05, -15.03) * mm, v(-0.04, -15.74) * mm, v(-0.49, -16.42) * mm, v(-1.42, -16.8) * mm, v(-2.53, -16.62) * mm, v(-3.31, -16.05) * mm, v(-3.54, -15.54) * mm], "startDerivative": vector(-5.48, 7.37) * mm, "endDerivative": vector(-2.6, 8.78) * mm});
            skLineSegment(sketch, "E324", {"start": v(13.26, -15.44) * mm, "end": v(13.92, -15.28) * mm});
            skLineSegment(sketch, "E325", {"start": v(15.95, -13.3) * mm, "end": v(16.74, -13.14) * mm});
            skFitSpline(sketch, "E326", {"points": [v(16.74, -13.14) * mm, v(16.5, -12.59) * mm, v(15, -12.02) * mm, v(13.51, -12.67) * mm, v(13.33, -13.39) * mm, v(13.58, -14.08) * mm, v(14.39, -14.72) * mm, v(15.35, -14.85) * mm, v(15.7, -15.04) * mm, v(15.83, -15.31) * mm, v(15.65, -15.77) * mm, v(15.15, -15.96) * mm, v(14.55, -15.88) * mm, v(13.92, -15.28) * mm], "startDerivative": vector(-1.49, 8.18) * mm, "endDerivative": vector(-7.28, 8.95) * mm});
            skFitSpline(sketch, "E327", {"points": [v(15.95, -13.3) * mm, v(15.61, -12.94) * mm, v(15.08, -12.81) * mm, v(14.53, -12.89) * mm, v(14.23, -13.14) * mm, v(14.25, -13.42) * mm, v(14.7, -13.72) * mm, v(15.45, -13.84) * mm, v(16.12, -14.12) * mm, v(16.57, -14.44) * mm, v(16.75, -14.92) * mm, v(16.76, -15.63) * mm, v(16.31, -16.32) * mm, v(15.38, -16.7) * mm, v(14.27, -16.51) * mm, v(13.49, -15.94) * mm, v(13.26, -15.44) * mm], "startDerivative": vector(-5.48, 7.37) * mm, "endDerivative": vector(-2.6, 8.78) * mm});
            skLineSegment(sketch, "E328", {"start": v(10.03, -14.08) * mm, "end": v(11.54, -14.08) * mm});
            skFitSpline(sketch, "E329", {"points": [v(11.54, -14.08) * mm, v(11.54, -13.63) * mm, v(11.24, -13.13) * mm, v(10.69, -12.97) * mm, v(10.19, -13.13) * mm, v(10, -13.55) * mm, v(10.03, -14.08) * mm], "startDerivative": vector(0.34, 2.82) * mm, "endDerivative": vector(0.38, -3.19) * mm});
            skLineSegment(sketch, "E330", {"start": v(12.7, -14.72) * mm, "end": v(9.77, -14.72) * mm});
            skFitSpline(sketch, "E331", {"points": [v(9.77, -14.72) * mm, v(10, -15.49) * mm, v(10.49, -15.97) * mm, v(10.95, -16.04) * mm, v(11.58, -15.42) * mm], "startDerivative": vector(0.58, -3.06) * mm, "endDerivative": vector(2.19, 3) * mm});
            skLineSegment(sketch, "E332", {"start": v(11.58, -15.42) * mm, "end": v(12.54, -15.42) * mm});
            skEllipticalArc(sketch, "E333", {});
            skLineSegment(sketch, "E334", {"start": v(3.77, -12.18) * mm, "end": v(3.77, -16.61) * mm});
            skLineSegment(sketch, "E335", {"start": v(3.77, -16.61) * mm, "end": v(4.83, -16.61) * mm});
            skLineSegment(sketch, "E336", {"start": v(4.83, -16.61) * mm, "end": v(4.83, -13.77) * mm});
            skLineSegment(sketch, "E337", {"start": v(3.77, -12.18) * mm, "end": v(4.71, -12.18) * mm});
            skLineSegment(sketch, "E338", {"start": v(4.71, -12.18) * mm, "end": v(4.71, -12.57) * mm});
            skFitSpline(sketch, "E339", {"points": [v(4.71, -12.57) * mm, v(5.04, -12.32) * mm, v(5.56, -12.08) * mm, v(6.3, -12.2) * mm], "startDerivative": vector(1.08, 0.84) * mm, "endDerivative": vector(1.92, -0.6) * mm});
            skLineSegment(sketch, "E340", {"start": v(6.3, -12.2) * mm, "end": v(6.3, -13.01) * mm});
            skFitSpline(sketch, "E341", {"points": [v(6.3, -13.01) * mm, v(5.9, -12.95) * mm, v(5.33, -13.1) * mm, v(4.88, -13.45) * mm, v(4.83, -13.77) * mm], "startDerivative": vector(-1.63, 0.4) * mm, "endDerivative": vector(0.05, -1.56) * mm});
            skLineSegment(sketch, "E342", {"start": v(-4.45, -12.26) * mm, "end": v(-4.45, -16.69) * mm});
            skLineSegment(sketch, "E343", {"start": v(-4.45, -16.69) * mm, "end": v(-5.33, -16.69) * mm});
            skLineSegment(sketch, "E344", {"start": v(-4.45, -12.26) * mm, "end": v(-5.35, -12.26) * mm});
            skLineSegment(sketch, "E345", {"start": v(-5.35, -12.26) * mm, "end": v(-5.35, -15.35) * mm});
            skFitSpline(sketch, "E346", {"points": [v(-5.35, -15.35) * mm, v(-5.69, -15.7) * mm, v(-6.23, -15.96) * mm, v(-6.74, -15.7) * mm, v(-7.1, -15.35) * mm], "startDerivative": vector(-1.24, -1.52) * mm, "endDerivative": vector(-1.41, 1.47) * mm});
            skLineSegment(sketch, "E347", {"start": v(-7.1, -15.35) * mm, "end": v(-7.1, -12.26) * mm});
            skPoint(sketch, "E347.endSnap0", {"position": v(-4.9, -12.26) * mm});
            skLineSegment(sketch, "E348", {"start": v(-7.1, -12.26) * mm, "end": v(-8.18, -12.26) * mm});
            skLineSegment(sketch, "E349", {"start": v(-8.18, -12.26) * mm, "end": v(-8.18, -15.35) * mm});
            skLineSegment(sketch, "E350", {"start": v(-5.33, -16.69) * mm, "end": v(-5.33, -16.33) * mm});
            skFitSpline(sketch, "E351", {"points": [v(-8.18, -15.35) * mm, v(-7.96, -16.33) * mm, v(-7.24, -16.69) * mm, v(-6.37, -16.73) * mm, v(-5.8, -16.6) * mm, v(-5.33, -16.33) * mm], "startDerivative": vector(0.28, -4.86) * mm, "endDerivative": vector(2.64, 1.84) * mm});
            skLineSegment(sketch, "E352", {"start": v(-9.33, -10.39) * mm, "end": v(-9.33, -16.54) * mm});
            skLineSegment(sketch, "E353", {"start": v(-9.33, -10.39) * mm, "end": v(-10.3, -10.39) * mm});
            skLineSegment(sketch, "E354", {"start": v(-10.3, -10.39) * mm, "end": v(-10.3, -12.36) * mm});
            skEllipse(sketch, "E355", {"center": v(-11.37, -14.38) * mm, "majorRadius": 1.54 * mm, "minorRadius": 0.94 * mm, "majorAxis": v(0, -1)});
            skEllipticalArc(sketch, "E356", {});
            skLineSegment(sketch, "E357", {"start": v(-9.33, -16.54) * mm, "end": v(-10.12, -16.54) * mm});
            skLineSegment(sketch, "E358", {"start": v(-10.12, -16.54) * mm, "end": v(-10.12, -16.21) * mm});
            skLineSegment(sketch, "E359", {"start": v(33.56, 10.27) * mm, "end": v(30.24, 16.22) * mm});
            skLineSegment(sketch, "E360", {"start": v(30.24, 16.22) * mm, "end": v(18.66, 16.22) * mm});
            skLineSegment(sketch, "E361", {"start": v(18.66, 16.22) * mm, "end": v(18.66, 23.85) * mm});
            skLineSegment(sketch, "E362", {"start": v(18.66, 23.85) * mm, "end": v(15.2, 23.85) * mm});
            skLineSegment(sketch, "E363", {"start": v(15.2, 23.85) * mm, "end": v(15.2, 34.27) * mm});
            skLineSegment(sketch, "E364", {"start": v(15.2, 34.27) * mm, "end": v(3, 34.27) * mm});
            skLineSegment(sketch, "E365", {"start": v(3, 34.27) * mm, "end": v(3, 30.18) * mm});
            skLineSegment(sketch, "E366", {"start": v(3, 30.18) * mm, "end": v(2.1, 29.27) * mm});
            skLineSegment(sketch, "E367", {"start": v(2.1, 29.27) * mm, "end": v(2.1, 43.4) * mm});
            skLineSegment(sketch, "E368", {"start": v(2.1, 43.4) * mm, "end": v(10.72, 43.43) * mm});
            skLineSegment(sketch, "E369", {"start": v(10.72, 43.43) * mm, "end": v(10.72, 45.2) * mm});
            skLineSegment(sketch, "E370", {"start": v(10.72, 45.2) * mm, "end": v(-2, 45.16) * mm});
            skLineSegment(sketch, "E371", {"start": v(-2, 45.16) * mm, "end": v(-1.94, 27) * mm});
            skLineSegment(sketch, "E372", {"start": v(-1.94, 27) * mm, "end": v(-3.6, 25.61) * mm});
            skLineSegment(sketch, "E373", {"start": v(-3.6, 25.61) * mm, "end": v(-3.6, 48.07) * mm});
            skLineSegment(sketch, "E374", {"start": v(-3.6, 48.07) * mm, "end": v(10.8, 48.07) * mm});
            skLineSegment(sketch, "E375", {"start": v(10.8, 48.07) * mm, "end": v(10.8, 50.26) * mm});
            skLineSegment(sketch, "E376", {"start": v(10.8, 50.26) * mm, "end": v(-9.5, 50.26) * mm});
            skLineSegment(sketch, "E377", {"start": v(-9.5, 50.26) * mm, "end": v(-9.5, 21.47) * mm});
            skLineSegment(sketch, "E378", {"start": v(-9.5, 21.47) * mm, "end": v(-16.9, 15.97) * mm});
            skLineSegment(sketch, "E379", {"start": v(-16.9, 15.97) * mm, "end": v(-27.9, 15.97) * mm});
            skLineSegment(sketch, "E380", {"start": v(-27.9, 15.97) * mm, "end": v(-30.86, 9.38) * mm});
            skLineSegment(sketch, "E381", {"start": v(-30.86, 9.38) * mm, "end": v(-29.22, 9.38) * mm});
            skLineSegment(sketch, "E382", {"start": v(-29.22, 9.38) * mm, "end": v(-29.22, 6.12) * mm});
            skLineSegment(sketch, "E383", {"start": v(-29.22, 6.12) * mm, "end": v(31.15, 6.12) * mm});
            skLineSegment(sketch, "E384", {"start": v(31.15, 6.12) * mm, "end": v(31.15, 10.27) * mm});
            skLineSegment(sketch, "E385", {"start": v(31.15, 10.27) * mm, "end": v(33.56, 10.27) * mm});
            skLineSegment(sketch, "E386", {"start": v(-8.52, 18.65) * mm, "end": v(-8.52, 17.55) * mm});
            skLineSegment(sketch, "E387", {"start": v(-8.52, 17.55) * mm, "end": v(-11.3, 15.87) * mm});
            skLineSegment(sketch, "E388", {"start": v(-11.3, 15.87) * mm, "end": v(-12.47, 15.87) * mm});
            skLineSegment(sketch, "E389", {"start": v(-12.47, 15.87) * mm, "end": v(-12.47, 16.53) * mm});
            skLineSegment(sketch, "E390", {"start": v(-12.47, 16.53) * mm, "end": v(-8.52, 18.95) * mm});
            skLineSegment(sketch, "E391", {"start": v(-8.52, 18.95) * mm, "end": v(-8.52, 18.65) * mm});
            skLineSegment(sketch, "E392", {"start": v(-3.4, 19.25) * mm, "end": v(-1.44, 20.76) * mm});
            skLineSegment(sketch, "E393", {"start": v(-1.44, 20.76) * mm, "end": v(-1.44, 15.82) * mm});
            skLineSegment(sketch, "E394", {"start": v(-1.44, 15.82) * mm, "end": v(-3.4, 15.82) * mm});
            skLineSegment(sketch, "E395", {"start": v(-3.4, 15.82) * mm, "end": v(-3.4, 19.25) * mm});
            skLineSegment(sketch, "E396", {"start": v(-1.62, 23.83) * mm, "end": v(-1.62, 22.62) * mm});
            skLineSegment(sketch, "E397", {"start": v(-1.62, 22.62) * mm, "end": v(-3.26, 21.86) * mm});
            skLineSegment(sketch, "E398", {"start": v(-3.26, 21.86) * mm, "end": v(-3.26, 22.78) * mm});
            skLineSegment(sketch, "E399", {"start": v(-3.26, 22.78) * mm, "end": v(-1.62, 23.83) * mm});
            skLineSegment(sketch, "E400", {"start": v(2.04, 25.73) * mm, "end": v(3.36, 26.46) * mm});
            skLineSegment(sketch, "E401", {"start": v(3.36, 26.46) * mm, "end": v(3.36, 27.49) * mm});
            skLineSegment(sketch, "E402", {"start": v(3.36, 27.49) * mm, "end": v(2.04, 26.55) * mm});
            skLineSegment(sketch, "E403", {"start": v(2.04, 26.55) * mm, "end": v(2.04, 25.73) * mm});
            skLineSegment(sketch, "E404", {"start": v(3.49, 24.58) * mm, "end": v(3.49, 16.2) * mm});
            skLineSegment(sketch, "E405", {"start": v(3.49, 16.2) * mm, "end": v(2.14, 16.2) * mm});
            skLineSegment(sketch, "E406", {"start": v(2.14, 16.2) * mm, "end": v(2.14, 23.75) * mm});
            skLineSegment(sketch, "E407", {"start": v(2.14, 23.75) * mm, "end": v(3.49, 24.58) * mm});
            skLineSegment(sketch, "E408", {"start": v(13.12, 22.17) * mm, "end": v(16.87, 22.17) * mm});
            skLineSegment(sketch, "E409", {"start": v(16.87, 22.17) * mm, "end": v(16.87, 15.98) * mm});
            skLineSegment(sketch, "E410", {"start": v(16.87, 15.98) * mm, "end": v(4.83, 15.98) * mm});
            skLineSegment(sketch, "E411", {"start": v(4.83, 15.98) * mm, "end": v(4.83, 32.95) * mm});
            skLineSegment(sketch, "E412", {"start": v(4.83, 32.95) * mm, "end": v(13.08, 32.95) * mm});
            skLineSegment(sketch, "E413", {"start": v(13.08, 32.95) * mm, "end": v(13.12, 22.17) * mm});
            skLineSegment(sketch, "E414.bottom", {"start": v(29.96, 7.2) * mm, "end": v(27.88, 7.2) * mm});
            skLineSegment(sketch, "E414.top", {"start": v(29.96, 9.94) * mm, "end": v(27.88, 9.94) * mm});
            skLineSegment(sketch, "E414.left", {"start": v(29.96, 7.2) * mm, "end": v(29.96, 9.94) * mm});
            skLineSegment(sketch, "E414.right", {"start": v(27.88, 7.2) * mm, "end": v(27.88, 9.94) * mm});
            skPoint(sketch, "E414.middle", {"position": v(28.92, 8.57) * mm});
            skLineSegment(sketch, "E415.1.0.0", {"start": v(26.33, 9.94) * mm, "end": v(24.25, 9.94) * mm});
            skLineSegment(sketch, "E415.1.0.1", {"start": v(26.33, 7.2) * mm, "end": v(26.33, 9.94) * mm});
            skLineSegment(sketch, "E415.1.0.2", {"start": v(24.25, 7.2) * mm, "end": v(24.25, 9.94) * mm});
            skLineSegment(sketch, "E415.1.0.3", {"start": v(26.33, 7.2) * mm, "end": v(24.25, 7.2) * mm});
            skLineSegment(sketch, "E415.2.0.0", {"start": v(22.7, 9.94) * mm, "end": v(20.62, 9.94) * mm});
            skLineSegment(sketch, "E415.2.0.1", {"start": v(22.7, 7.2) * mm, "end": v(22.7, 9.94) * mm});
            skLineSegment(sketch, "E415.2.0.2", {"start": v(20.62, 7.2) * mm, "end": v(20.62, 9.94) * mm});
            skLineSegment(sketch, "E415.2.0.3", {"start": v(22.7, 7.2) * mm, "end": v(20.62, 7.2) * mm});
            skLineSegment(sketch, "E415.3.0.0", {"start": v(19.07, 9.94) * mm, "end": v(16.99, 9.94) * mm});
            skLineSegment(sketch, "E415.3.0.1", {"start": v(19.07, 7.2) * mm, "end": v(19.07, 9.94) * mm});
            skLineSegment(sketch, "E415.3.0.2", {"start": v(16.99, 7.2) * mm, "end": v(16.99, 9.94) * mm});
            skLineSegment(sketch, "E415.3.0.3", {"start": v(19.07, 7.2) * mm, "end": v(16.99, 7.2) * mm});
            skLineSegment(sketch, "E415.4.0.0", {"start": v(15.44, 9.94) * mm, "end": v(13.36, 9.94) * mm});
            skLineSegment(sketch, "E415.4.0.1", {"start": v(15.44, 7.2) * mm, "end": v(15.44, 9.94) * mm});
            skLineSegment(sketch, "E415.4.0.2", {"start": v(13.36, 7.2) * mm, "end": v(13.36, 9.94) * mm});
            skLineSegment(sketch, "E415.4.0.3", {"start": v(15.44, 7.2) * mm, "end": v(13.36, 7.2) * mm});
            skLineSegment(sketch, "E415.5.0.0", {"start": v(11.8, 9.94) * mm, "end": v(9.73, 9.94) * mm});
            skLineSegment(sketch, "E415.5.0.1", {"start": v(11.8, 7.2) * mm, "end": v(11.8, 9.94) * mm});
            skLineSegment(sketch, "E415.5.0.2", {"start": v(9.73, 7.2) * mm, "end": v(9.73, 9.94) * mm});
            skLineSegment(sketch, "E415.5.0.3", {"start": v(11.8, 7.2) * mm, "end": v(9.73, 7.2) * mm});
            skLineSegment(sketch, "E415.6.0.0", {"start": v(8.18, 9.94) * mm, "end": v(6.1, 9.94) * mm});
            skLineSegment(sketch, "E415.6.0.1", {"start": v(8.18, 7.2) * mm, "end": v(8.18, 9.94) * mm});
            skLineSegment(sketch, "E415.6.0.2", {"start": v(6.1, 7.2) * mm, "end": v(6.1, 9.94) * mm});
            skLineSegment(sketch, "E415.6.0.3", {"start": v(8.18, 7.2) * mm, "end": v(6.1, 7.2) * mm});
            skLineSegment(sketch, "E415.7.0.0", {"start": v(4.55, 9.94) * mm, "end": v(2.47, 9.94) * mm});
            skLineSegment(sketch, "E415.7.0.1", {"start": v(4.55, 7.2) * mm, "end": v(4.55, 9.94) * mm});
            skLineSegment(sketch, "E415.7.0.2", {"start": v(2.47, 7.2) * mm, "end": v(2.47, 9.94) * mm});
            skLineSegment(sketch, "E415.7.0.3", {"start": v(4.55, 7.2) * mm, "end": v(2.47, 7.2) * mm});
            skLineSegment(sketch, "E415.8.0.0", {"start": v(0.92, 9.94) * mm, "end": v(-1.16, 9.94) * mm});
            skLineSegment(sketch, "E415.8.0.1", {"start": v(0.92, 7.2) * mm, "end": v(0.92, 9.94) * mm});
            skLineSegment(sketch, "E415.8.0.2", {"start": v(-1.16, 7.2) * mm, "end": v(-1.16, 9.94) * mm});
            skLineSegment(sketch, "E415.8.0.3", {"start": v(0.92, 7.2) * mm, "end": v(-1.16, 7.2) * mm});
            skLineSegment(sketch, "E415.9.0.0", {"start": v(-2.71, 9.94) * mm, "end": v(-4.8, 9.94) * mm});
            skLineSegment(sketch, "E415.9.0.1", {"start": v(-2.71, 7.2) * mm, "end": v(-2.71, 9.94) * mm});
            skLineSegment(sketch, "E415.9.0.2", {"start": v(-4.8, 7.2) * mm, "end": v(-4.8, 9.94) * mm});
            skLineSegment(sketch, "E415.9.0.3", {"start": v(-2.71, 7.2) * mm, "end": v(-4.8, 7.2) * mm});
            skLineSegment(sketch, "E415.10.0.0", {"start": v(-6.34, 9.94) * mm, "end": v(-8.42, 9.94) * mm});
            skLineSegment(sketch, "E415.10.0.1", {"start": v(-6.34, 7.2) * mm, "end": v(-6.34, 9.94) * mm});
            skLineSegment(sketch, "E415.10.0.2", {"start": v(-8.42, 7.2) * mm, "end": v(-8.42, 9.94) * mm});
            skLineSegment(sketch, "E415.10.0.3", {"start": v(-6.34, 7.2) * mm, "end": v(-8.42, 7.2) * mm});
            skLineSegment(sketch, "E415.11.0.0", {"start": v(-9.97, 9.94) * mm, "end": v(-12.05, 9.94) * mm});
            skLineSegment(sketch, "E415.11.0.1", {"start": v(-9.97, 7.2) * mm, "end": v(-9.97, 9.94) * mm});
            skLineSegment(sketch, "E415.11.0.2", {"start": v(-12.05, 7.2) * mm, "end": v(-12.05, 9.94) * mm});
            skLineSegment(sketch, "E415.11.0.3", {"start": v(-9.97, 7.2) * mm, "end": v(-12.05, 7.2) * mm});
            skLineSegment(sketch, "E415.12.0.0", {"start": v(-13.6, 9.94) * mm, "end": v(-15.68, 9.94) * mm});
            skLineSegment(sketch, "E415.12.0.1", {"start": v(-13.6, 7.2) * mm, "end": v(-13.6, 9.94) * mm});
            skLineSegment(sketch, "E415.12.0.2", {"start": v(-15.68, 7.2) * mm, "end": v(-15.68, 9.94) * mm});
            skLineSegment(sketch, "E415.12.0.3", {"start": v(-13.6, 7.2) * mm, "end": v(-15.68, 7.2) * mm});
            skLineSegment(sketch, "E415.13.0.0", {"start": v(-17.23, 9.94) * mm, "end": v(-19.31, 9.94) * mm});
            skLineSegment(sketch, "E415.13.0.1", {"start": v(-17.23, 7.2) * mm, "end": v(-17.23, 9.94) * mm});
            skLineSegment(sketch, "E415.13.0.2", {"start": v(-19.31, 7.2) * mm, "end": v(-19.31, 9.94) * mm});
            skLineSegment(sketch, "E415.13.0.3", {"start": v(-17.23, 7.2) * mm, "end": v(-19.31, 7.2) * mm});
            skLineSegment(sketch, "E415.14.0.0", {"start": v(-20.86, 9.94) * mm, "end": v(-22.94, 9.94) * mm});
            skLineSegment(sketch, "E415.14.0.1", {"start": v(-20.86, 7.2) * mm, "end": v(-20.86, 9.94) * mm});
            skLineSegment(sketch, "E415.14.0.2", {"start": v(-22.94, 7.2) * mm, "end": v(-22.94, 9.94) * mm});
            skLineSegment(sketch, "E415.14.0.3", {"start": v(-20.86, 7.2) * mm, "end": v(-22.94, 7.2) * mm});
            skLineSegment(sketch, "E415.15.0.0", {"start": v(-24.5, 9.94) * mm, "end": v(-26.57, 9.94) * mm});
            skLineSegment(sketch, "E415.15.0.1", {"start": v(-24.5, 7.2) * mm, "end": v(-24.5, 9.94) * mm});
            skLineSegment(sketch, "E415.15.0.2", {"start": v(-26.57, 7.2) * mm, "end": v(-26.57, 9.94) * mm});
            skLineSegment(sketch, "E415.15.0.3", {"start": v(-24.5, 7.2) * mm, "end": v(-26.57, 7.2) * mm});
            skLineSegment(sketch, "E415.direction1", {"start": v(27.88, 7.2) * mm, "end": v(24.25, 7.2) * mm, "construction": true});
            skLineSegment(sketch, "E416", {"start": v(36.43, -16.76) * mm, "end": v(30.35, -16.76) * mm, "construction": true});
            const initialGuessF0  = {"E278": [0.022455972619354725, -0.013476599007844925, 0, -1, 0.0021808426827192307, 0.001522037420786693, 2.123347976248809, 1.0826615455431157], "E279": [0.022455972619354725, -0.013476599007844925, 0, -1, 0.003252852879256027, 0.002614517221200075, 2.1256952424376676, 1.0993472911521682], "E308": [0.03966698236763477, -0.014480842277407646, 0, -1, 0.0024184565991163254, 0.002076530967662523, 5.869879304150575, 3.6888386389978107], "E333": [0.010778111638501287, -0.014414461329579353, 0, -1, 0.002391548827290535, 0.0019375099645474968, 1.4446437207658351, 1.1356500662066504], "E356": [-0.011366505175828934, -0.01438143290579319, 0, 1, 0.002453448250889778, 0.0018729588959092581, 5.679789931569453, 3.8712000995785165]};
            skSetInitialGuess(sketch, initialGuessF0);
            skSolve(sketch);
        }
        {
            var Q0;
            Q0=qCreatedBy(makeId("Top.planeOp"),FACE);
            var sketch = newSketch(context, id + "F1", { "sketchPlane" : qUnion([Q0])});
            skLineSegment(sketch, "E417.bottom", {"start": v(58.46, -22.97) * mm, "end": v(-58.46, -22.97) * mm});
            skLineSegment(sketch, "E417.right", {"start": v(-58.46, -22.97) * mm, "end": v(-58.46, 54.27) * mm});
            skLineSegment(sketch, "E418.0", {"start": v(17.93, 55.26) * mm, "end": v(-17.93, 55.26) * mm});
            skLineSegment(sketch, "E419", {"start": v(58.46, 4.22) * mm, "end": v(42.05, 4.22) * mm});
            skLineSegment(sketch, "E420.0", {"start": v(-27.9, 15.97) * mm, "end": v(-30.86, 9.38) * mm, "construction": true});
            skPoint(sketch, "E421", {"position": v(0, 55.26) * mm});
            skLineSegment(sketch, "E422", {"start": v(17.93, 55.26) * mm, "end": v(42.05, 4.22) * mm});
            skLineSegment(sketch, "E423", {"start": v(-17.93, 55.26) * mm, "end": v(-42.05, 4.22) * mm});
            skLineSegment(sketch, "E424", {"start": v(17.93, 55.26) * mm, "end": v(0, 93.18) * mm, "construction": true});
            skLineSegment(sketch, "E425", {"start": v(-17.93, 55.26) * mm, "end": v(0, 93.18) * mm, "construction": true});
            skLineSegment(sketch, "E426", {"start": v(58.46, -22.97) * mm, "end": v(58.46, 4.22) * mm});
            skLineSegment(sketch, "E427.trimOffspring", {"start": v(-42.05, 4.22) * mm, "end": v(-58.46, 4.22) * mm});
            skSolve(sketch);
        }
        {
            var Q0;
            Q0 = qSketchRegion(id + "F1", true);
            extrude(context, id + "F2", {"entities" : qUnion([Q0]), "oppositeDirection" : true, "depth" : 4 * mm});
        }
        {
            var Q0;
            Q0 = qSketchRegion(id + "F0", true);
            extrude(context, id + "F3", {"entities" : qUnion([Q0]), "operationType" : NewBodyOperationType.ADD, "depth" : 2 * mm});
        }
        {
            var Q0;
            Q0=makeQuery(id+"F2.opExtrude","CAP_FACE",FACE,{"disambiguationData":[OSD([sQuery(id+"F1.wireOp",EDGE,"E417.bottom"),sQuery(id+"F1.wireOp",EDGE,"E417.right"),sQuery(id+"F1.wireOp",EDGE,"E418.0"),sQuery(id+"F1.wireOp",EDGE,"E419"),sQuery(id+"F1.wireOp",EDGE,"E422"),sQuery(id+"F1.wireOp",EDGE,"E423"),sQuery(id+"F1.wireOp",EDGE,"E426"),sQuery(id+"F1.wireOp",EDGE,"E427.trimOffspring")])],"isStart":false});
            var sketch = newSketch(context, id + "F4", { "sketchPlane" : qUnion([Q0])});
            skArc(sketch, "E428", {"start": v(-16.8, -21.27) * mm, "mid": v(-12, -12.42) * mm, "end": v(-20.83, -7.61) * mm});
            skArc(sketch, "E429", {"start": v(-16.8, -21.27) * mm, "mid": v(-5.21, -16.54) * mm, "end": v(-9.44, -4.76) * mm});
            skArc(sketch, "E430", {"start": v(-3.47, -29.43) * mm, "mid": v(2.32, -15.29) * mm, "end": v(-8.77, -4.76) * mm});
            skArc(sketch, "E431", {"start": v(-3.47, -29.43) * mm, "mid": v(7.85, -17.86) * mm, "end": v(-1.08, -4.36) * mm});
            skArc(sketch, "E432", {"start": v(17.77, -24.74) * mm, "mid": v(14.58, -9.67) * mm, "end": v(0.3, -3.92) * mm});
            skArc(sketch, "E433", {"start": v(17.77, -24.74) * mm, "mid": v(18.69, -5.17) * mm, "end": v(-0.84, -3.61) * mm});
            skArc(sketch, "E434", {"start": v(20.66, 0) * mm, "mid": v(19.31, 1.48) * mm, "end": v(17.96, 0) * mm});
            skArc(sketch, "E435", {"start": v(20.66, 0) * mm, "mid": v(19.31, 2.56) * mm, "end": v(17.96, 0) * mm});
            skArc(sketch, "E436", {"start": v(16.46, 0) * mm, "mid": v(15.11, 1.48) * mm, "end": v(13.76, 0) * mm});
            skArc(sketch, "E437", {"start": v(16.46, 0) * mm, "mid": v(15.11, 2.56) * mm, "end": v(13.76, 0) * mm});
            skLineSegment(sketch, "E438", {"start": v(0.3, -3.92) * mm, "end": v(-1.08, -4.36) * mm});
            skLineSegment(sketch, "E439", {"start": v(-1.85, -4.14) * mm, "end": v(-0.84, -3.61) * mm});
            skArc(sketch, "E440.trimOffspring", {"start": v(-1.85, -4.14) * mm, "mid": v(-5.4, -3.76) * mm, "end": v(-8.91, -4.37) * mm});
            skLineSegment(sketch, "E441", {"start": v(-8.77, -4.76) * mm, "end": v(-9.44, -4.76) * mm});
            skLineSegment(sketch, "E442", {"start": v(-9.99, -4.52) * mm, "end": v(-8.91, -4.37) * mm});
            skArc(sketch, "E443.trimOffspring", {"start": v(-9.99, -4.52) * mm, "mid": v(-15.95, -4.17) * mm, "end": v(-20.83, -7.61) * mm});
            skSolve(sketch);
        }
        {
            var Q0;
            Q0 = qSketchRegion(id + "F4", true);
            extrude(context, id + "F5", {"entities" : qUnion([Q0]), "operationType" : NewBodyOperationType.REMOVE, "oppositeDirection" : true, "depth" : 0.5 * mm});
        }
        {
            var Q0;
            Q0=makeQuery(id+"F3.opExtrude","SWEPT_EDGE",EDGE,{"disambiguationData":[OSD([sQuery(id+"F0.wireOp",EDGE,"E293"),sQuery(id+"F0.wireOp",EDGE,"E294")])]});
            fillet(context, id + "F6", {"entities" : qUnion([Q0]), "radius" : 1 * mm, "tangentPropagation" : true, "allowEdgeOverflow" : false});
        }
    });
